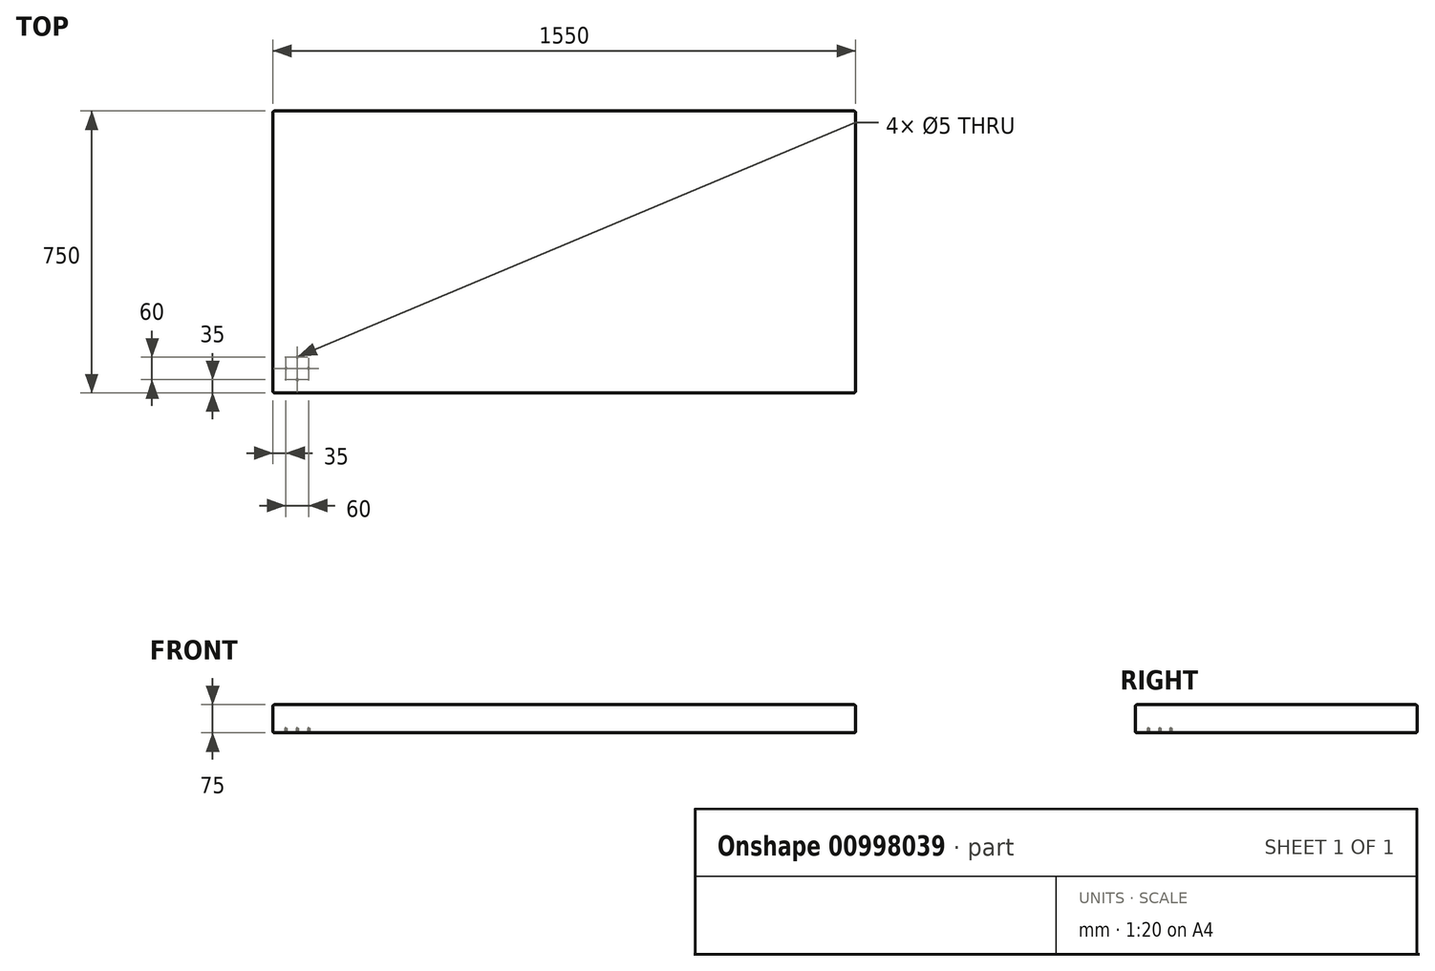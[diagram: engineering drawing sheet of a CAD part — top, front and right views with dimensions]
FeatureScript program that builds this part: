
annotation { "Feature Type Name" : "Feature", "Feature Type Description" : "" }
export const myFeature = defineFeature(function(context is Context, id is Id, definition is map)
    precondition{}
    {
        {
            var Q0;
            Q0=qCreatedBy(makeId("Top.planeOp"),FACE);
            var sketch = newSketch(context, id + "F0", { "sketchPlane" : qUnion([Q0])});
            skLineSegment(sketch, "E0.bottom", {"start": v(-775, 375) * mm, "end": v(775, 375) * mm});
            skLineSegment(sketch, "E0.top", {"start": v(-775, -375) * mm, "end": v(775, -375) * mm});
            skLineSegment(sketch, "E0.left", {"start": v(-775, 375) * mm, "end": v(-775, -375) * mm});
            skLineSegment(sketch, "E0.right", {"start": v(775, 375) * mm, "end": v(775, -375) * mm});
            skSolve(sketch);
        }
        {
            var Q0;
            Q0=makeQuery(id+"F0.imprint","IMPRINT",FACE,{"disambiguationData":[TD([[makeQuery(id+"F0.imprint","IMPRINT",EDGE,{"derivedFrom":sQuery(id+"F0.wireOp",EDGE,"E0.bottom")}),-1.0]])]});
            extrude(context, id + "F1", {"entities" : qUnion([Q0]), "depth" : 50 * mm, "offsetDistance" : 25.4 * mm});
        }
        {
            var Q0;
            Q0=makeQuery(id+"F1.opExtrude","CAP_FACE",FACE,{"disambiguationData":[OSD([sQuery(id+"F0.wireOp",EDGE,"E0.bottom"),sQuery(id+"F0.wireOp",EDGE,"E0.top"),sQuery(id+"F0.wireOp",EDGE,"E0.left"),sQuery(id+"F0.wireOp",EDGE,"E0.right")])],"isStart":true});
            extrude(context, id + "F2", {"entities" : qUnion([Q0]), "operationType" : NewBodyOperationType.ADD, "depth" : 25 * mm, "offsetDistance" : 25 * mm});
        }
        {
            var Q0;
            {var subQ0=sQuery(id+"F0.wireOp",EDGE,"E0.left");var subQ1=sQuery(id+"F0.wireOp",EDGE,"E0.top");Q0=makeQuery(id+"F2.boolean.opBoolean","MERGE",EDGE,{"derivedFrom":[makeQuery(id+"F1.opExtrude","SWEPT_EDGE",EDGE,{"disambiguationData":[OSD([subQ1,subQ0])]}),makeQuery(id+"F2.opExtrude","SWEPT_EDGE",EDGE,{"disambiguationData":[OSD([subQ1,subQ0])]})]});}
            var Q1;
            Q1=makeQuery(id+"F1.opExtrude","CAP_EDGE",EDGE,{"disambiguationData":[OSD([sQuery(id+"F0.wireOp",EDGE,"E0.top")])],"isStart":false});
            var Q2;
            Q2=makeQuery(id+"F2.opExtrude","CAP_EDGE",EDGE,{"disambiguationData":[OSD([sQuery(id+"F0.wireOp",EDGE,"E0.top")])],"isStart":false});
            var Q3;
            Q3=makeQuery(id+"F2.opExtrude","CAP_EDGE",EDGE,{"disambiguationData":[OSD([sQuery(id+"F0.wireOp",EDGE,"E0.left")])],"isStart":false});
            var Q4;
            Q4=makeQuery(id+"F1.opExtrude","CAP_EDGE",EDGE,{"disambiguationData":[OSD([sQuery(id+"F0.wireOp",EDGE,"E0.left")])],"isStart":false});
            var Q5;
            {var subQ0=sQuery(id+"F0.wireOp",EDGE,"E0.left");var subQ1=sQuery(id+"F0.wireOp",EDGE,"E0.bottom");Q5=makeQuery(id+"F2.boolean.opBoolean","MERGE",EDGE,{"derivedFrom":[makeQuery(id+"F1.opExtrude","SWEPT_EDGE",EDGE,{"disambiguationData":[OSD([subQ1,subQ0])]}),makeQuery(id+"F2.opExtrude","SWEPT_EDGE",EDGE,{"disambiguationData":[OSD([subQ1,subQ0])]})]});}
            var Q6;
            {var subQ0=sQuery(id+"F0.wireOp",EDGE,"E0.right");var subQ1=sQuery(id+"F0.wireOp",EDGE,"E0.top");Q6=makeQuery(id+"F2.boolean.opBoolean","MERGE",EDGE,{"derivedFrom":[makeQuery(id+"F1.opExtrude","SWEPT_EDGE",EDGE,{"disambiguationData":[OSD([subQ1,subQ0])]}),makeQuery(id+"F2.opExtrude","SWEPT_EDGE",EDGE,{"disambiguationData":[OSD([subQ1,subQ0])]})]});}
            var Q7;
            Q7=makeQuery(id+"F1.opExtrude","CAP_EDGE",EDGE,{"disambiguationData":[OSD([sQuery(id+"F0.wireOp",EDGE,"E0.right")])],"isStart":false});
            var Q8;
            Q8=makeQuery(id+"F2.opExtrude","CAP_EDGE",EDGE,{"disambiguationData":[OSD([sQuery(id+"F0.wireOp",EDGE,"E0.right")])],"isStart":false});
            var Q9;
            {var subQ0=sQuery(id+"F0.wireOp",EDGE,"E0.right");var subQ1=sQuery(id+"F0.wireOp",EDGE,"E0.bottom");Q9=makeQuery(id+"F2.boolean.opBoolean","MERGE",EDGE,{"derivedFrom":[makeQuery(id+"F1.opExtrude","SWEPT_EDGE",EDGE,{"disambiguationData":[OSD([subQ1,subQ0])]}),makeQuery(id+"F2.opExtrude","SWEPT_EDGE",EDGE,{"disambiguationData":[OSD([subQ1,subQ0])]})]});}
            var Q10;
            Q10=makeQuery(id+"F2.opExtrude","CAP_EDGE",EDGE,{"disambiguationData":[OSD([sQuery(id+"F0.wireOp",EDGE,"E0.bottom")])],"isStart":false});
            var Q11;
            Q11=makeQuery(id+"F1.opExtrude","CAP_EDGE",EDGE,{"disambiguationData":[OSD([sQuery(id+"F0.wireOp",EDGE,"E0.bottom")])],"isStart":false});
            fillet(context, id + "F3", {"entities" : qUnion([Q0, Q1, Q2, Q3, Q4, Q5, Q6, Q7, Q8, Q9, Q10, Q11]), "radius" : 5 * mm, "tangentPropagation" : true, "allowEdgeOverflow" : false});
        }
        {
            var Q0;
            Q0=makeQuery(id+"F2.opExtrude","CAP_FACE",FACE,{"disambiguationData":[OSD([sQuery(id+"F0.wireOp",EDGE,"E0.bottom"),sQuery(id+"F0.wireOp",EDGE,"E0.top"),sQuery(id+"F0.wireOp",EDGE,"E0.left"),sQuery(id+"F0.wireOp",EDGE,"E0.right")])],"isStart":false});
            var sketch = newSketch(context, id + "F4", { "sketchPlane" : qUnion([Q0])});
            skCircle(sketch, "E1", {"center": v(-710, 310) * mm, "radius": 10 * mm, "construction": true});
            skCircle(sketch, "E2", {"center": v(-710, 340) * mm, "radius": 3 * mm});
            skCircle(sketch, "E3.1.0", {"center": v(-740, 310) * mm, "radius": 3 * mm});
            skCircle(sketch, "E3.2.0", {"center": v(-710, 280) * mm, "radius": 3 * mm});
            skCircle(sketch, "E3.3.0", {"center": v(-680, 310) * mm, "radius": 3 * mm});
            skSolve(sketch);
        }
        {
            var Q0;
            Q0=sQuery(id+"FI2u4w4qJAGE9kw_1.1.F4.wireOp",VERTEX,"E2.center");
            var Q1;
            Q1=sQuery(id+"FI2u4w4qJAGE9kw_1.1.F4.wireOp",VERTEX,"E3.1.0.center");
            var Q2;
            Q2=sQuery(id+"FI2u4w4qJAGE9kw_1.1.F4.wireOp",VERTEX,"E3.2.0.center");
            var Q3;
            Q3=sQuery(id+"FI2u4w4qJAGE9kw_1.1.F4.wireOp",VERTEX,"E3.3.0.center");
            var Q4;
            Q4=sQuery(id+"F4.wireOp",VERTEX,"E2.center");
            var Q5;
            Q5=sQuery(id+"F4.wireOp",VERTEX,"E3.2.0.center");
            var Q6;
            Q6=sQuery(id+"F4.wireOp",VERTEX,"E3.3.0.center");
            var Q7;
            Q7=sQuery(id+"F4.wireOp",VERTEX,"E3.1.0.center");
            var Q8;
            Q8=sQuery(id+"FyFHS3QoGTKHiL0_1.1.F4.wireOp",VERTEX,"E3.2.0.center");
            var Q9;
            Q9=sQuery(id+"FyFHS3QoGTKHiL0_1.1.F4.wireOp",VERTEX,"E3.3.0.center");
            var Q10;
            Q10=sQuery(id+"FyFHS3QoGTKHiL0_1.1.F4.wireOp",VERTEX,"E2.center");
            var Q11;
            Q11=sQuery(id+"FyFHS3QoGTKHiL0_1.1.F4.wireOp",VERTEX,"E3.1.0.center");
            var Q12;
            Q12=sQuery(id+"FyFHS3QoGTKHiL0_1.1.FI2u4w4qJAGE9kw_1.1.F4.wireOp",VERTEX,"E3.1.0.center");
            var Q13;
            Q13=sQuery(id+"FyFHS3QoGTKHiL0_1.1.FI2u4w4qJAGE9kw_1.1.F4.wireOp",VERTEX,"E3.2.0.center");
            var Q14;
            Q14=sQuery(id+"FyFHS3QoGTKHiL0_1.1.FI2u4w4qJAGE9kw_1.1.F4.wireOp",VERTEX,"E3.3.0.center");
            var Q15;
            Q15=sQuery(id+"FyFHS3QoGTKHiL0_1.1.FI2u4w4qJAGE9kw_1.1.F4.wireOp",VERTEX,"E2.center");
            var Q16;
            Q16=makeQuery(id+"F1.opExtrude","SWEPT_BODY",BODY,{"disambiguationData":[OSD([sQuery(id+"F0.wireOp",EDGE,"E0.bottom"),sQuery(id+"F0.wireOp",EDGE,"E0.top"),sQuery(id+"F0.wireOp",EDGE,"E0.left"),sQuery(id+"F0.wireOp",EDGE,"E0.right")])]});
            hole(context, id + "F5", {"style" : HoleStyle.SIMPLE, "endStyle" : HoleEndStyle.BLIND, "holeDiameter" : 5 * mm, "majorDiameter" : 5 * mm, "holeDepth" : 12 * mm, "isTappedThrough" : true, "tappedDepth" : 12 * mm, "tapClearance" : 3, "locations" : qUnion([Q0, Q1, Q2, Q3, Q4, Q5, Q6, Q7, Q8, Q9, Q10, Q11, Q12, Q13, Q14, Q15]), "scope" : qUnion([Q16])});
        }
    });
